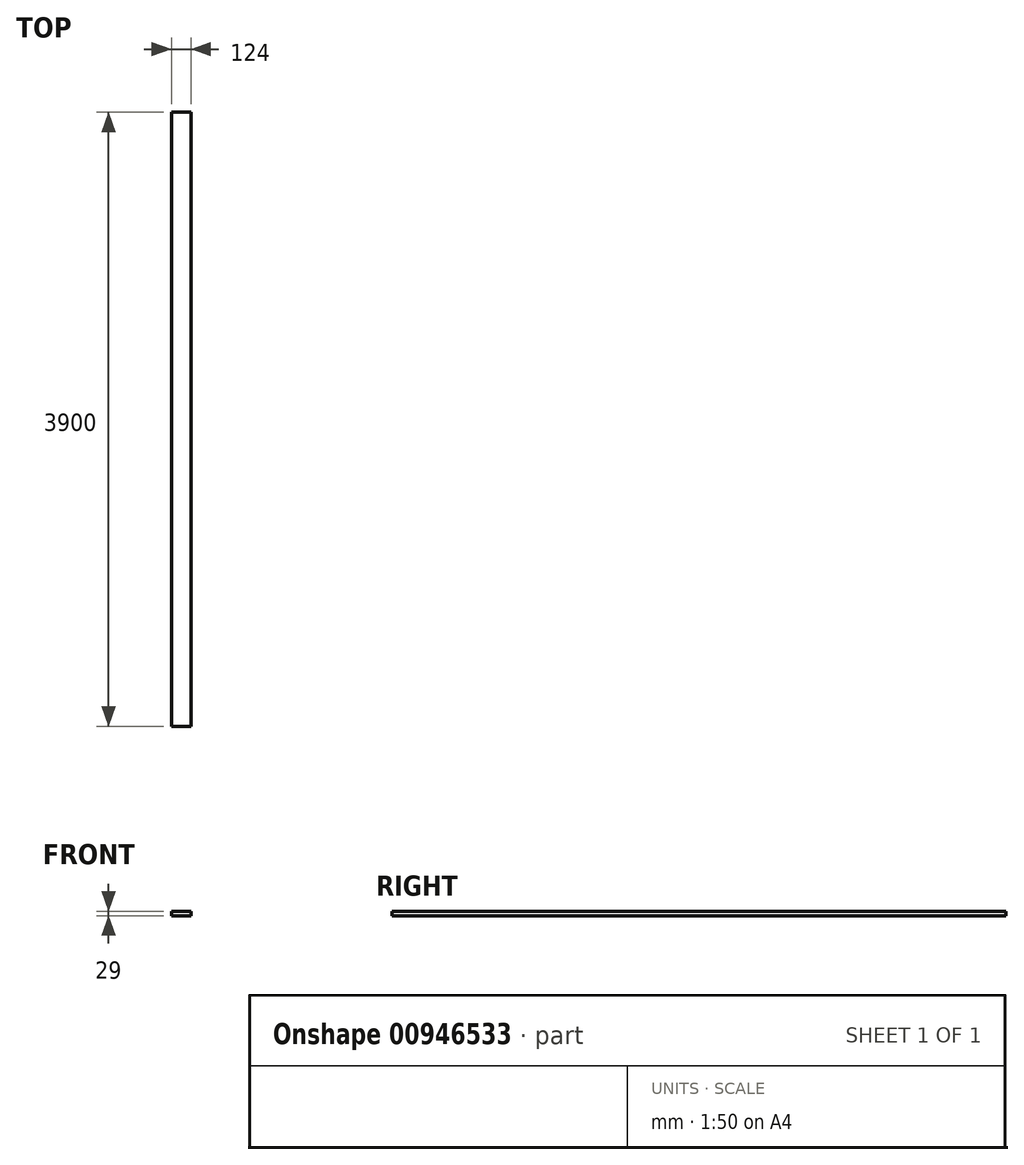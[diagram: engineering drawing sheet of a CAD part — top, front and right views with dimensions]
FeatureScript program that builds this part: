
annotation { "Feature Type Name" : "Feature", "Feature Type Description" : "" }
export const myFeature = defineFeature(function(context is Context, id is Id, definition is map)
    precondition{}
    {
        {
            var Q0;
            Q0=qCreatedBy(makeId("Front.planeOp"),FACE);
            var sketch = newSketch(context, id + "F0", { "sketchPlane" : qUnion([Q0])});
            skLineSegment(sketch, "E0.bottom", {"start": v(0, 0) * mm, "end": v(124, 0) * mm});
            skLineSegment(sketch, "E0.top", {"start": v(0, 29) * mm, "end": v(124, 29) * mm});
            skLineSegment(sketch, "E0.left", {"start": v(0, 0) * mm, "end": v(0, 29) * mm});
            skLineSegment(sketch, "E0.right", {"start": v(124, 0) * mm, "end": v(124, 29) * mm});
            skSolve(sketch);
        }
        {
            var Q0;
            Q0=qSketchRegion(id+"F0",true);
            extrude(context, id + "F1", {"entities" : qUnion([Q0]), "depth" : 3900 * mm, "offsetDistance" : 25 * mm});
        }
    });
